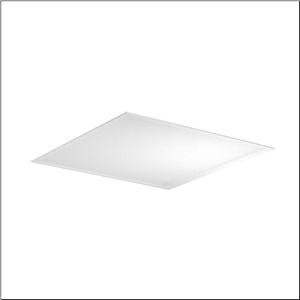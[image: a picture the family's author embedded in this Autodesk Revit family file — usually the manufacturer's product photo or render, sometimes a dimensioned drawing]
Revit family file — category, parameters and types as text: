
# Revit family: apollon_r__21_square_51mq12wc2454_9269
name_source: partatom
category: Lighting Fixtures
units: mm (PartAtom-declared; Revit-internal decimal feet)

## family parameters
Cut with Voids When Loaded = No
Host = Face
Light Source = No
Part Type = Normal
Room Calculation Point = No
Round Connector Dimension = Use Diameter
Shared = No

## types (1)
- Apollon® 21 square (1 x LED, 4200 lm, 24.7 W, 4000K)
    Apparent Load = 25 VA
    CIE Flux Codes = 60 87 97 100 100
    Color Rendering = 80
    Color Temperature = 4000K
    Default Elevation = 1800 mm
    Description = Apollon® 21 square, office luminaire, primary optical cover: micro prismatic cover, of PMMA, CAT 2 (L<= 3000cd/m²), light emission: direct distribution, primary light characteristic: symmetric, installation type: lay-in mounting, LED, rated luminous flux: 4.200lm, luminous efficacy: 170lm/W, light colour: 840, colour temperature: 4000K, with terminal, 5-pole, mains connection: 220..240V, AC/DC, 0/50..60Hz, rated input power: 24.7W, housing, of aluminium, coated, traffic white (RAL 9016), module: M600, length: 595mm, width: 595mm, height: 30mm, housing upper side, of sheet steel, galvanised, protection rating (complete): IP20, protection rating (lamp compartment, on room side): IP54, insulation class (complete): insulation class II (safety insulation), certification: CE, ENEC, impact resistance: IK03, permissible operating ambient temperature: -20..+45°C, permissible storage temperature: -40..+80°C, packaging unit: 1 piece
    Height = 0 mm  [stored 0 ft]
    Lamp = 1 x LED
    Lamp Light Flux = 4200 lm
    Lamp Power = 24.7 W
    Lamp count = 1
    Length = 595 mm
    Luminous efficacy = 170 lm/W
    Manufacturer = Siteco
    ModVariant = No
    Model = 51MQ12WC2454
    Mounting Place = Ceiling
    Mounting Type = Recessed
    Number of Poles = 1
    OnlyDefault = Yes
    Power Factor = 1
    Product Name = Apollon® 21 square
    Product group = office luminaire | ceiling recessed
    ProductGroupID = 401
    Protection Class = Protection class II
    Protection Degree = IP 20
    RLX_Detail_Level = 1
    RLX_Emergency_Light_Flux = 0 lm
    RLX_Emergency_Type = 0
    RLX_Emergency_Type_DB = No
    RlxData = <blob elided: 12493 chars, md5=f8f287b8>
    Socket = socket
    Standby Power = 0 W
    System Light Flux = 4200 lm
    System Power = 25 W
    Type Comments = Product without accessories
    Type Image = l_1291049.jpg
    URL = http://relux.com
    VarID = ---
    Voltage = 0 V
    Weight = 0.00 kg
    Width = 595 mm

note: [stored X ft] marks values corroborated as IEEE doubles in the binary element streams (Revit-internal decimal feet)

## geometry (parser evidence)
native form markers: Sweep x11
no freeform markers — native parametric forms only
